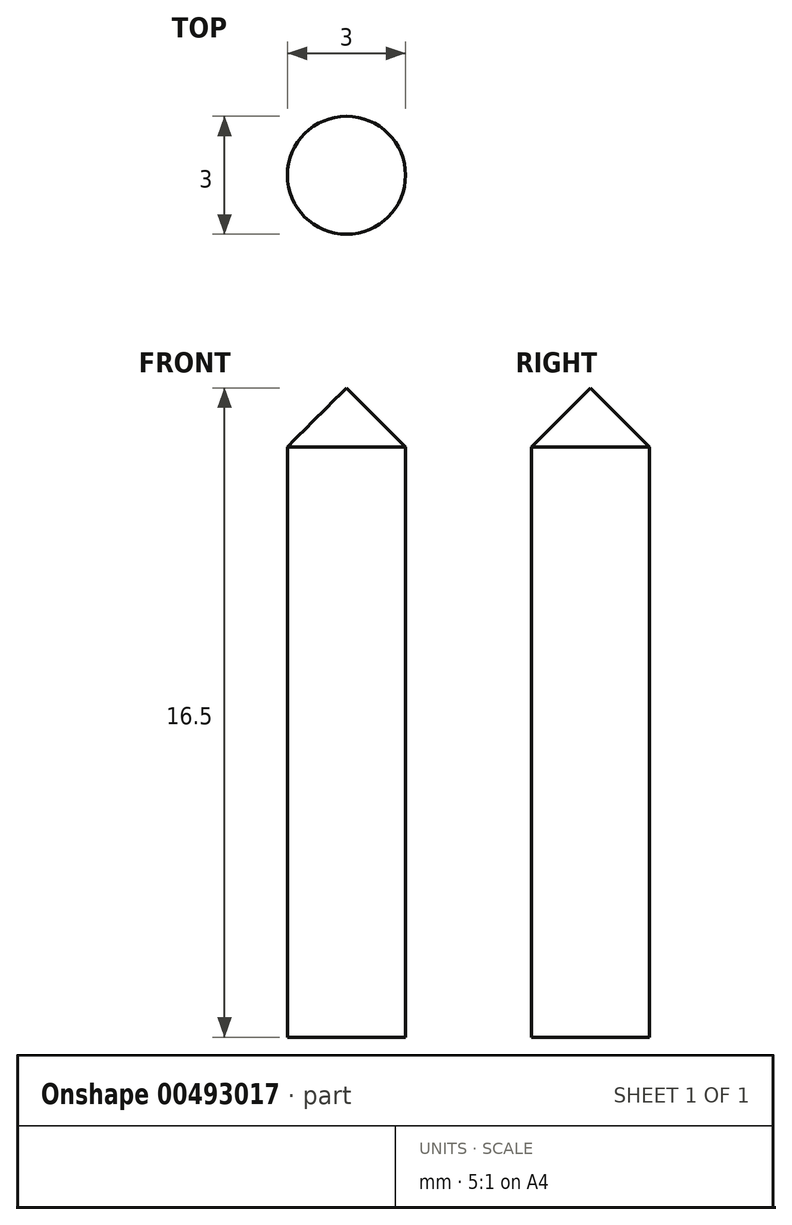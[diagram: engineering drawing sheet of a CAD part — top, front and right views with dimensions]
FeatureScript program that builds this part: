
annotation { "Feature Type Name" : "Feature", "Feature Type Description" : "" }
export const myFeature = defineFeature(function(context is Context, id is Id, definition is map)
    precondition{}
    {
        {
            var Q0;
            Q0=qCreatedBy(makeId("Top.planeOp"),FACE);
            var sketch = newSketch(context, id + "F0", { "sketchPlane" : qUnion([Q0])});
            skCircle(sketch, "E0", {"center": v(0, 0) * mm, "radius": 1.5 * mm});
            skSolve(sketch);
        }
        {
            var Q0;
            Q0 = qSketchRegion(id + "F0", true);
            extrude(context, id + "F1", {"entities" : qUnion([Q0]), "depth" : 15 * mm});
        }
        {
            var Q0;
            Q0=qCreatedBy(makeId("Front.planeOp"),FACE);
            var sketch = newSketch(context, id + "F2", { "sketchPlane" : qUnion([Q0])});
            skLineSegment(sketch, "E1", {"start": v(0, 15) * mm, "end": v(0, 16.5) * mm});
            skLineSegment(sketch, "E2", {"start": v(0, 16.5) * mm, "end": v(1.5, 15) * mm});
            skLineSegment(sketch, "E3", {"start": v(1.5, 15) * mm, "end": v(0, 15) * mm});
            skSolve(sketch);
        }
        {
            var Q0;
            Q0 = qSketchRegion(id + "F2", true);
            var Q1;
            Q1=sQuery(id+"F2.wireOp",EDGE,"E1");
            revolve(context, id + "F3", {"operationType" : NewBodyOperationType.ADD, "entities" : qUnion([Q0]), "axis" : qUnion([Q1]), "revolveType" : RevolveType.FULL});
        }
    });
